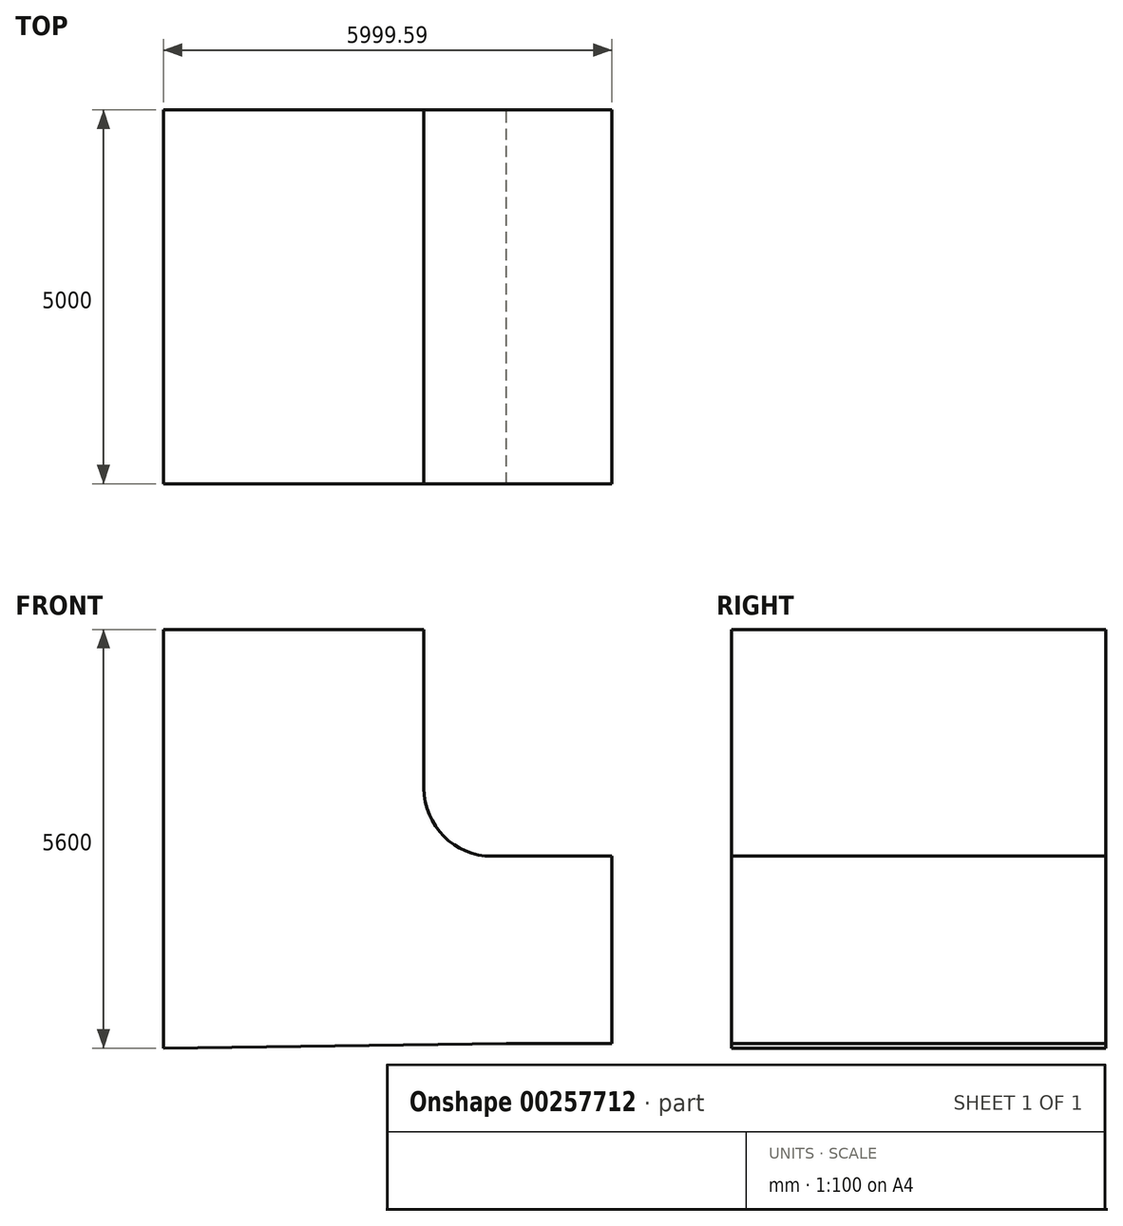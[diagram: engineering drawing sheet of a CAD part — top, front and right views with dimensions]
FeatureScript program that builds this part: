
annotation { "Feature Type Name" : "Feature", "Feature Type Description" : "" }
export const myFeature = defineFeature(function(context is Context, id is Id, definition is map)
    precondition{}
    {
        {
            var Q0;
            Q0=qCreatedBy(makeId("Front.planeOp"),FACE);
            var sketch = newSketch(context, id + "F0", { "sketchPlane" : qUnion([Q0])});
            skLineSegment(sketch, "E0", {"start": v(-618.9, 5538.74) * mm, "end": v(-618.9, -61.26) * mm});
            skLineSegment(sketch, "E1", {"start": v(-618.9, -61.26) * mm, "end": v(3970.69, 0) * mm});
            skLineSegment(sketch, "E2", {"start": v(3970.69, 0) * mm, "end": v(4880.69, 0) * mm});
            skLineSegment(sketch, "E3", {"start": v(4880.69, 0) * mm, "end": v(5380.69, 0) * mm});
            skLineSegment(sketch, "E4", {"start": v(5380.69, 0) * mm, "end": v(5380.69, 2505) * mm});
            skLineSegment(sketch, "E5", {"start": v(-618.9, 5538.74) * mm, "end": v(2866.1, 5538.74) * mm});
            skPoint(sketch, "E6.visualSharp", {"position": v(3766.1, 2505) * mm});
            skPoint(sketch, "E7.visualSharp", {"position": v(4216.1, 2955) * mm});
            skPoint(sketch, "E8.end.orphan", {"position": v(4666.1, 3405) * mm});
            skPoint(sketch, "E9.start.orphan", {"position": v(5380.69, 3405) * mm});
            skPoint(sketch, "E10.end.orphan", {"position": v(5380.69, 2955) * mm});
            skLineSegment(sketch, "E11", {"start": v(2866.1, 5538.74) * mm, "end": v(2866.1, 3415) * mm});
            skPoint(sketch, "E12.end.orphan", {"position": v(3316.1, 5538.74) * mm});
            skPoint(sketch, "E13.start.orphan", {"position": v(3766.1, 5538.74) * mm});
            skLineSegment(sketch, "E14", {"start": v(2866.1, 5538.74) * mm, "end": v(3316.1, 5538.74) * mm});
            skLineSegment(sketch, "E15", {"start": v(3766.1, 5538.74) * mm, "end": v(3316.1, 5538.74) * mm});
            skLineSegment(sketch, "E16", {"start": v(5380.69, 2505) * mm, "end": v(5380.69, 2955) * mm});
            skLineSegment(sketch, "E17", {"start": v(5380.69, 3405) * mm, "end": v(5380.69, 2955) * mm});
            skLineSegment(sketch, "E18", {"start": v(5380.69, 3405) * mm, "end": v(3766.1, 3405) * mm});
            skLineSegment(sketch, "E19", {"start": v(3766.1, 3405) * mm, "end": v(3766.1, 5538.74) * mm});
            skPoint(sketch, "E20.visualSharp", {"position": v(2866.1, 2505) * mm});
            skPoint(sketch, "E21.start.orphan", {"position": v(3316.1, 2955) * mm});
            skLineSegment(sketch, "E22", {"start": v(3316.1, 5538.74) * mm, "end": v(3316.1, 3410) * mm});
            skLineSegment(sketch, "E23", {"start": v(5380.69, 2955) * mm, "end": v(3771.1, 2955) * mm});
            skLineSegment(sketch, "E24", {"start": v(2866.1, 3415) * mm, "end": v(2866.1, 3415) * mm});
            skArc(sketch, "E25.filletArc", {"start": v(3316.1, 3410) * mm, "mid": v(3449.36, 3088.27) * mm, "end": v(3771.1, 2955) * mm});
            skArc(sketch, "E26.filletArc", {"start": v(2866.1, 3415) * mm, "mid": v(3132.63, 2771.53) * mm, "end": v(3776.1, 2505) * mm});
            skLineSegment(sketch, "E27", {"start": v(2866.1, 5538.74) * mm, "end": v(2866.1, 5248.74) * mm});
            skLineSegment(sketch, "E28", {"start": v(2866.1, 4958.74) * mm, "end": v(2866.1, 4668.74) * mm});
            skLineSegment(sketch, "E29", {"start": v(2866.1, 4668.74) * mm, "end": v(2866.1, 4378.74) * mm});
            skLineSegment(sketch, "E30", {"start": v(2866.1, 4378.74) * mm, "end": v(2866.1, 4088.74) * mm});
            skLineSegment(sketch, "E31", {"start": v(2866.1, 4088.74) * mm, "end": v(2866.1, 3798.74) * mm});
            skLineSegment(sketch, "E32", {"start": v(2866.1, 3798.74) * mm, "end": v(3766.1, 3798.74) * mm});
            skLineSegment(sketch, "E33", {"start": v(2866.1, 4088.74) * mm, "end": v(3766.1, 4088.74) * mm});
            skLineSegment(sketch, "E34", {"start": v(2866.1, 4378.74) * mm, "end": v(3766.1, 4378.74) * mm});
            skLineSegment(sketch, "E35", {"start": v(2866.1, 4668.74) * mm, "end": v(3766.1, 4668.74) * mm});
            skLineSegment(sketch, "E36", {"start": v(2866.1, 4958.74) * mm, "end": v(3766.1, 4958.74) * mm});
            skLineSegment(sketch, "E37", {"start": v(2866.1, 5248.74) * mm, "end": v(3766.1, 5248.74) * mm});
            skLineSegment(sketch, "E38", {"start": v(3766.1, 5538.74) * mm, "end": v(3816.1, 5538.74) * mm});
            skLineSegment(sketch, "E39", {"start": v(3816.1, 5538.74) * mm, "end": v(3816.1, 3455) * mm});
            skLineSegment(sketch, "E40", {"start": v(5380.69, 3405) * mm, "end": v(5380.69, 3455) * mm});
            skLineSegment(sketch, "E41", {"start": v(5380.69, 3455) * mm, "end": v(3816.1, 3455) * mm});
            skLineSegment(sketch, "E42.trimOffspring", {"start": v(4288.4, 2505) * mm, "end": v(3776.1, 2505) * mm});
            skPoint(sketch, "E43.start.orphan", {"position": v(4868.4, 2505) * mm});
            skPoint(sketch, "E44.trimOffspring.end.orphan", {"position": v(4578.4, 2505) * mm});
            skPoint(sketch, "E45.end.orphan", {"position": v(5090.69, 2505) * mm});
            skLineSegment(sketch, "E46", {"start": v(5380.69, 2505) * mm, "end": v(4288.4, 2505) * mm});
            skLineSegment(sketch, "E47", {"start": v(5380.69, 2955) * mm, "end": v(5090.69, 2955) * mm});
            skLineSegment(sketch, "E48", {"start": v(5090.69, 2955) * mm, "end": v(4800.69, 2955) * mm});
            skLineSegment(sketch, "E49", {"start": v(4800.69, 2955) * mm, "end": v(4575.9, 2955) * mm});
            skLineSegment(sketch, "E50", {"start": v(4575.9, 2955) * mm, "end": v(4285.9, 2955) * mm});
            skLineSegment(sketch, "E51", {"start": v(5090.69, 2955) * mm, "end": v(5090.69, 2505) * mm});
            skLineSegment(sketch, "E52", {"start": v(5090.69, 2955) * mm, "end": v(5090.69, 3405) * mm});
            skLineSegment(sketch, "E53", {"start": v(4800.69, 2955) * mm, "end": v(4800.69, 3405) * mm});
            skLineSegment(sketch, "E54", {"start": v(4800.69, 2955) * mm, "end": v(4800.69, 2505) * mm});
            skLineSegment(sketch, "E55", {"start": v(4800.69, 2505) * mm, "end": v(4510.69, 2505) * mm});
            skLineSegment(sketch, "E56", {"start": v(4510.69, 2505) * mm, "end": v(4510.69, 3405) * mm});
            skLineSegment(sketch, "E57", {"start": v(4510.69, 3405) * mm, "end": v(4220.69, 3405) * mm});
            skLineSegment(sketch, "E58", {"start": v(4220.69, 3405) * mm, "end": v(4220.69, 2505) * mm});
            skPoint(sketch, "E59.orphan", {"position": v(3816.1, 3405) * mm});
            skSolve(sketch);
        }
        {
            var Q0;
            Q0=makeQuery(id+"F0.imprint","IMPRINT",FACE,{"disambiguationData":[TD([[makeQuery(id+"F0.imprint","IMPRINT",EDGE,{"derivedFrom":sQuery(id+"F0.wireOp",EDGE,"E0")}),1.0]])]});
            extrude(context, id + "F1", {"entities" : qUnion([Q0]), "depth" : 5000 * mm});
        }
    });
